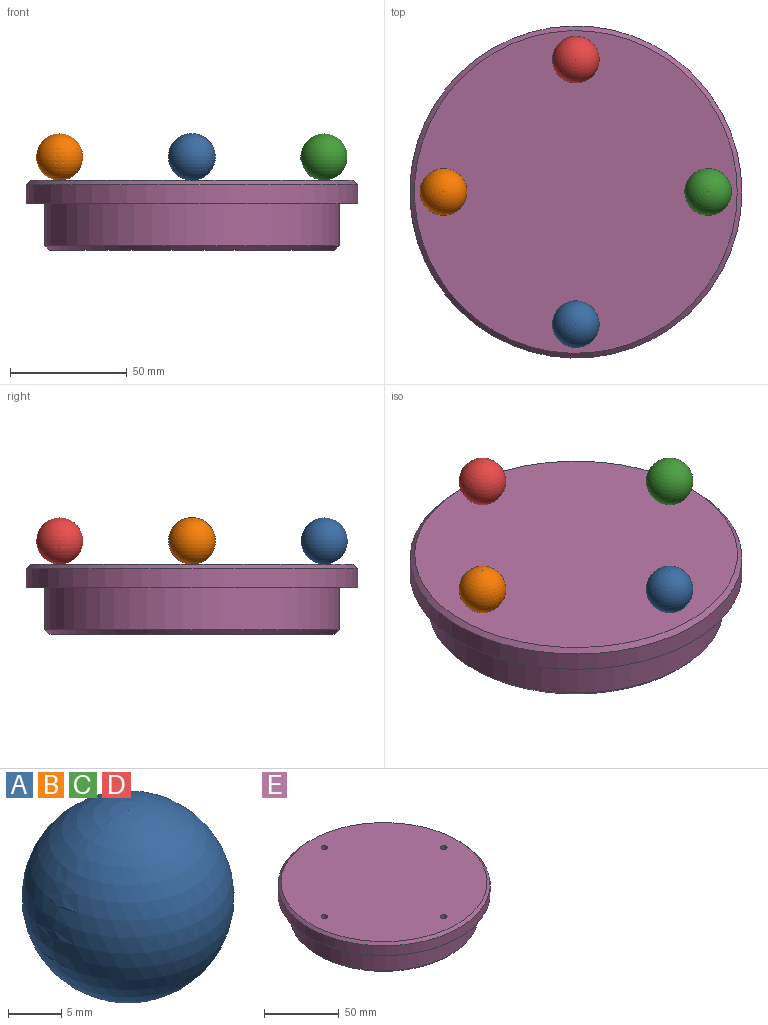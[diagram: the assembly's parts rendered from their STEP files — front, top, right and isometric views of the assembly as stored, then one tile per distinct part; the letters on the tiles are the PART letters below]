
ASSEMBLY  parts=5 mates=1
PART A: 2 faces, bbox 20x20x20 mm
  f0: plane 2x2mm, normal (0,0,-1), area 3.1mm2, adj f1
  f1: sphere r=10mm, area 1253.5mm2, adj f0
PART B: same geometry as A
PART C: same geometry as A
PART D: same geometry as A
PART E: 39 faces, bbox 142x142x30 mm
  f0: cylinder r=63mm len=126mm, axis (0,0,1), area 7125.1mm2, adj f4,f10
  f1: plane 122x122mm, normal (0,0,-1), area 11505.3mm2, adj f10,f12,f13,f14,f15,f16,f17,f19
  f2: cylinder r=71mm len=142mm, axis (0,0,-1), area 3568.8mm2, adj f4,f5
  f3: plane 138x138mm, normal (0,0,1), area 14899mm2, adj f5,f6,f7,f8,f9
  f4: plane 142x142mm, normal (0,0,-1), area 3367.8mm2, adj f0,f2
  f5: cone r=69mm half-angle=45deg, axis (0,0,-1), area 1244mm2, adj f2,f3
  f6: cylinder r=2.15mm len=10mm, axis (0,0,1), area 135.1mm2, adj f3,f32
  f7: cylinder r=2.15mm len=10mm, axis (0,0,1), area 135.1mm2, adj f3,f25
  f8: cylinder r=2.15mm len=10mm, axis (0,0,1), area 135.1mm2, adj f3,f18
  f9: cylinder r=2.15mm len=10mm, axis (0,0,1), area 135.1mm2, adj f3,f11
  f10: cone r=63mm half-angle=45deg, axis (0,0,1), area 1101.8mm2, adj f0,f1
  f11: plane 8.43x7.3mm, normal (0,0,-1), area 31.6mm2, adj f9,f12,f13,f14,f15,f16,f17
  f12: plane 20x4.21mm, normal (-1,0,0), area 84.3mm2, adj f1,f11,f13,f15
  f13: plane 20x3.65mm, normal (-0.5,0.87,0), area 84.3mm2, adj f1,f11,f12,f14
  f14: plane 20x3.65mm, normal (0.5,0.87,0), area 84.3mm2, adj f1,f11,f13,f16
  f15: plane 20x3.65mm, normal (-0.5,-0.87,0), area 84.3mm2, adj f1,f11,f12,f17
  f16: plane 20x4.21mm, normal (1,0,0), area 84.3mm2, adj f1,f11,f14,f17
  f17: plane 20x3.65mm, normal (0.5,-0.87,0), area 84.3mm2, adj f1,f11,f15,f16
  f18: plane 8.43x7.3mm, normal (0,0,-1), area 31.6mm2, adj f8,f19,f20,f21,f22,f23,f24
  f19: plane 20x4.21mm, normal (0,1,0), area 84.3mm2, adj f1,f18,f20,f22
  f20: plane 20x3.65mm, normal (0.87,0.5,0), area 84.3mm2, adj f1,f18,f19,f21
  f21: plane 20x3.65mm, normal (0.87,-0.5,0), area 84.3mm2, adj f1,f18,f20,f23
  f22: plane 20x3.65mm, normal (-0.87,0.5,0), area 84.3mm2, adj f1,f18,f19,f24
  f23: plane 20x4.21mm, normal (0,-1,0), area 84.3mm2, adj f1,f18,f21,f24
  f24: plane 20x3.65mm, normal (-0.87,-0.5,0), area 84.3mm2, adj f1,f18,f22,f23
  f25: plane 8.43x7.3mm, normal (0,0,-1), area 31.6mm2, adj f7,f26,f27,f28,f29,f30,f31
  f26: plane 20x4.21mm, normal (1,0,0), area 84.3mm2, adj f1,f25,f27,f29
  f27: plane 20x3.65mm, normal (0.5,-0.87,0), area 84.3mm2, adj f1,f25,f26,f28
  f28: plane 20x3.65mm, normal (-0.5,-0.87,0), area 84.3mm2, adj f1,f25,f27,f30
  f29: plane 20x3.65mm, normal (0.5,0.87,0), area 84.3mm2, adj f1,f25,f26,f31
  f30: plane 20x4.21mm, normal (-1,0,0), area 84.3mm2, adj f1,f25,f28,f31
  f31: plane 20x3.65mm, normal (-0.5,0.87,0), area 84.3mm2, adj f1,f25,f29,f30
  f32: plane 8.43x7.3mm, normal (0,0,-1), area 31.6mm2, adj f6,f33,f34,f35,f36,f37,f38
  f33: plane 20x4.21mm, normal (0,-1,0), area 84.3mm2, adj f1,f32,f34,f36
  f34: plane 20x3.65mm, normal (-0.87,-0.5,0), area 84.3mm2, adj f1,f32,f33,f35
  f35: plane 20x3.65mm, normal (-0.87,0.5,0), area 84.3mm2, adj f1,f32,f34,f37
  f36: plane 20x3.65mm, normal (0.87,-0.5,0), area 84.3mm2, adj f1,f32,f33,f38
  f37: plane 20x4.21mm, normal (0,1,0), area 84.3mm2, adj f1,f32,f35,f38
  f38: plane 20x3.65mm, normal (0.87,0.5,0), area 84.3mm2, adj f1,f32,f36,f37
PLACE A rot(axis=(0,0,1),180deg) t=(-32.67,-285.5,114.55)mm
PLACE B rot(axis=(0,0,1),90deg) t=(-34.3,-173.99,114.55)mm
PLACE C rot(axis=(0,0,-1),90deg) t=(78.84,-283.87,114.55)mm
PLACE D t=(77.21,-172.36,114.55)mm
PLACE E t=(22.27,-228.93,-362.68)mm
MATE parallel D.f0 <-> E.f8  axis (0,0,1) through (22.27,-172.36,147.32)mm
